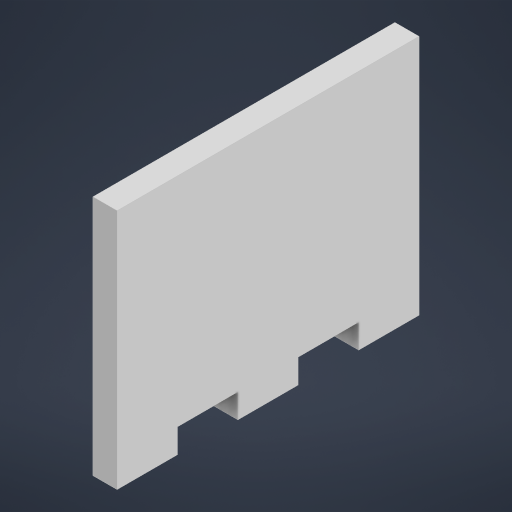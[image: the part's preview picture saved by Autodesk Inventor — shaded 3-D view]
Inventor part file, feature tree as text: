
AUTODESK INVENTOR PART (.ipt)
format: ipt  version: 2023.2 (Build 272271000, 271)  size: 199,168 bytes
history: native  units: mm
features: sketch x1
ambient origin geometry x8: Origin, YZ Plane, XZ Plane, XY Plane, X Axis, Y Axis, Z Axis, Center Point
bodies: Body1 (feature_tree)
feature tree (1):
  sketch  "Sketch1"  dims[d230=36.0mm d231=50.0mm d234=4.0mm d235=0.0mm d236=10.0mm d240=10.0mm d241=4.0mm d9=0.5mm d10=0.872665mm d11=0.5mm d12=0.872665mm d13=0.5mm d14=0.872665mm d27=0.5mm d28=0.872665mm d29=0.5mm d30=0.872665mm d88=0.5mm d89=0.872665mm d90=0.5mm d91=0.872665mm d116=0.5mm d117=0.872665mm d118=0.5mm d119=0.872665mm d154=0.5mm d155=0.872665mm d156=0.5mm d157=0.872665mm d181=0.5mm d182=0.872665mm d183=0.5mm d184=0.872665mm d221=0.5mm d222=0.872665mm d223=0.5mm d224=0.872665mm]
